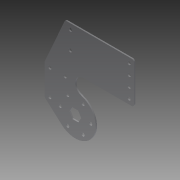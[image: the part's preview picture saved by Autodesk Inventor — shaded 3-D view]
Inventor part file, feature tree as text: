
AUTODESK INVENTOR PART (.ipt)
format: ipt  version: 2014 (Build 180170000, 170)  size: 165,376 bytes
history: native  units: in
note: dims shown in document units (in); Inventor stores cm internally (conversion verified against a paired STEP export)
features: extrude x2, fillet x1, sketch x1
ambient origin geometry x8: Origin, YZ Plane, XZ Plane, XY Plane, X Axis, Y Axis, Z Axis, Center Point
bodies: Solid1 (feature_tree)
feature tree (4):
  extrude  "Extrusion1"  Depth=0.125in
  extrude  "Extrusion2"  Depth=0.5in
  fillet  "Fillet2"  Radius=0.164in
  sketch  "Sketch2"  dims[d3=0.0625in d4=0.0in d7=0.625in d8=0.5in d23=0.164in d25=0.75in d26=0.0in d27=2.3622in d29=360.0deg d41=2.0in d42=0.75in d43=0.75in d44=1.5in d55=2.875in d57=0.164in d58=0.25in d59=0.25in d60=1.5748in d62=0.5in d63=0.3937in d65=1.0in d67=0.25in d68=1.444in d69=2.0in d70=1.5in d71=0.7833in d72=2.25in d76=2.2202in d78=0.25in d79=0.125in d82=0.7874in d84=0.75in d85=0.3937in d87=1.0in d91=1.25in d96=0.7874in d98=1.25in d99=0.3937in d101=1.0in d103=0.7874in d105=0.875in d106=0.3937in d108=1.0in d110=1.0in d111=1.0in d112=0.0in d113=0.25in d114=0.125in]
